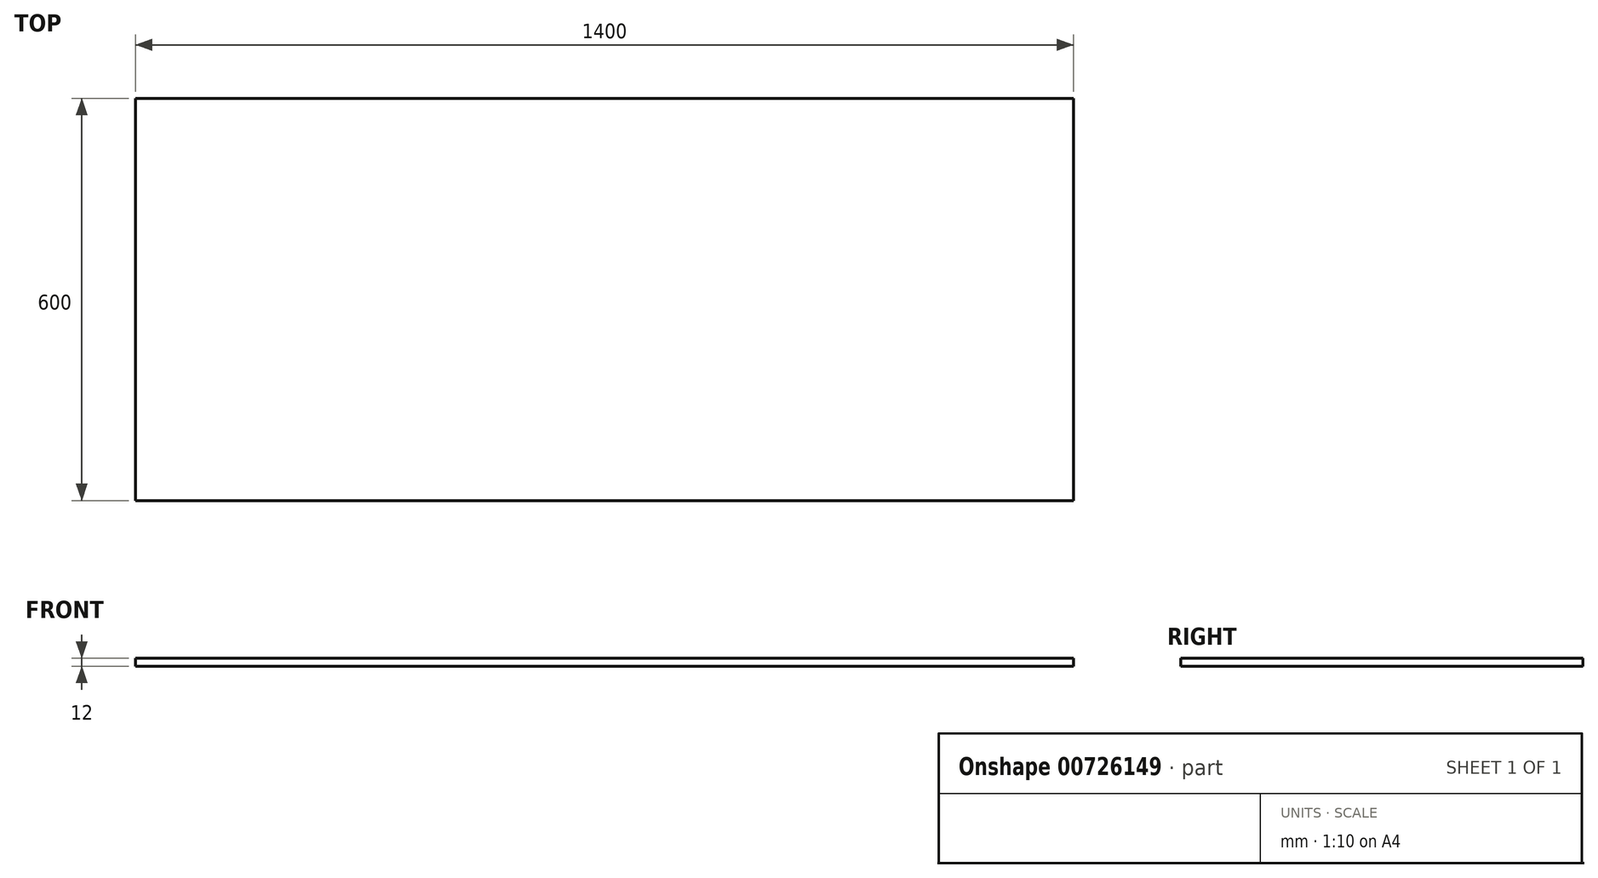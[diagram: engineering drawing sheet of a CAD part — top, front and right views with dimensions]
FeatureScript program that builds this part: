
annotation { "Feature Type Name" : "Feature", "Feature Type Description" : "" }
export const myFeature = defineFeature(function(context is Context, id is Id, definition is map)
    precondition{}
    {
        {
            var Q0;
            Q0=qCreatedBy(makeId("Top.planeOp"),FACE);
            var sketch = newSketch(context, id + "F0", { "sketchPlane" : qUnion([Q0])});
            skLineSegment(sketch, "E0.bottom", {"start": v(0, 0) * mm, "end": v(1400, 0) * mm});
            skLineSegment(sketch, "E0.top", {"start": v(0, 600) * mm, "end": v(1400, 600) * mm});
            skLineSegment(sketch, "E0.left", {"start": v(0, 0) * mm, "end": v(0, 600) * mm});
            skLineSegment(sketch, "E0.right", {"start": v(1400, 0) * mm, "end": v(1400, 600) * mm});
            skLineSegment(sketch, "E1", {"start": v(700, 600) * mm, "end": v(700, 0) * mm, "construction": true});
            skLineSegment(sketch, "E2", {"start": v(0, 300) * mm, "end": v(1400, 300) * mm, "construction": true});
            skSolve(sketch);
        }
        {
            var Q0;
            Q0 = qSketchRegion(id + "F0", true);
            extrude(context, id + "F1", {"entities" : qUnion([Q0]), "depth" : 12 * mm, "offsetDistance" : 25 * mm});
        }
    });
